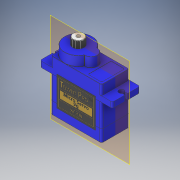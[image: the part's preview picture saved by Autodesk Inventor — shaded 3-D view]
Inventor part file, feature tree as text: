
AUTODESK INVENTOR PART (.ipt)
format: ipt  version: 2019 (Build 230136000, 136)  size: 1,556,480 bytes
history: native  units: in
note: dims shown in document units (in); Inventor stores cm internally (conversion verified against a paired STEP export)
features: other x13, plane x2, sketch x1
ambient origin geometry x8: Origin, YZ Plane, XZ Plane, XY Plane, X Axis, Y Axis, Z Axis, Center Point
bodies: Solid1 (feature_tree), Solid2 (feature_tree), Solid3 (feature_tree), Solid4 (feature_tree), Solid5 (feature_tree), Solid6 (feature_tree), Solid7 (feature_tree), Solid8 (feature_tree), Solid9 (feature_tree), Solid10 (feature_tree), Solid11 (feature_tree), Solid12 (feature_tree), Solid13 (feature_tree)
feature tree (16):
  plane  "Work Plane1"
  sketch  "Sketch1"  dims[d0=3.0in]
  plane  "Work Plane4"
  other  "SG90 - Micro Servo 9g - Tower Pro.1-1-solid1"
  other  "SG90 - Micro Servo 9g - Tower Pro.1-1-solid2"
  other  "SG90 - Micro Servo 9g - Tower Pro.1-1-solid3"
  other  "SG90 - Micro Servo 9g - Tower Pro.1-1-solid4"
  other  "SG90 - Micro Servo 9g - Tower Pro.1-1-solid5"
  other  "SG90 - Micro Servo 9g - Tower Pro.1-1-solid6"
  other  "SG90 - Micro Servo 9g - Tower Pro.1-1-solid7"
  other  "SG90 - Micro Servo 9g - Tower Pro.1-1-solid8"
  other  "SG90 - Micro Servo 9g - Tower Pro.1-1-solid9"
  other  "SG90 - Micro Servo 9g - Tower Pro.1-1-solid10"
  other  "SG90 - Micro Servo 9g - Tower Pro.1-1-solid11"
  other  "SG90 - Micro Servo 9g - Tower Pro.1-1-solid12"
  other  "SG90 - Micro Servo 9g - Tower Pro.1-1-solid13"
